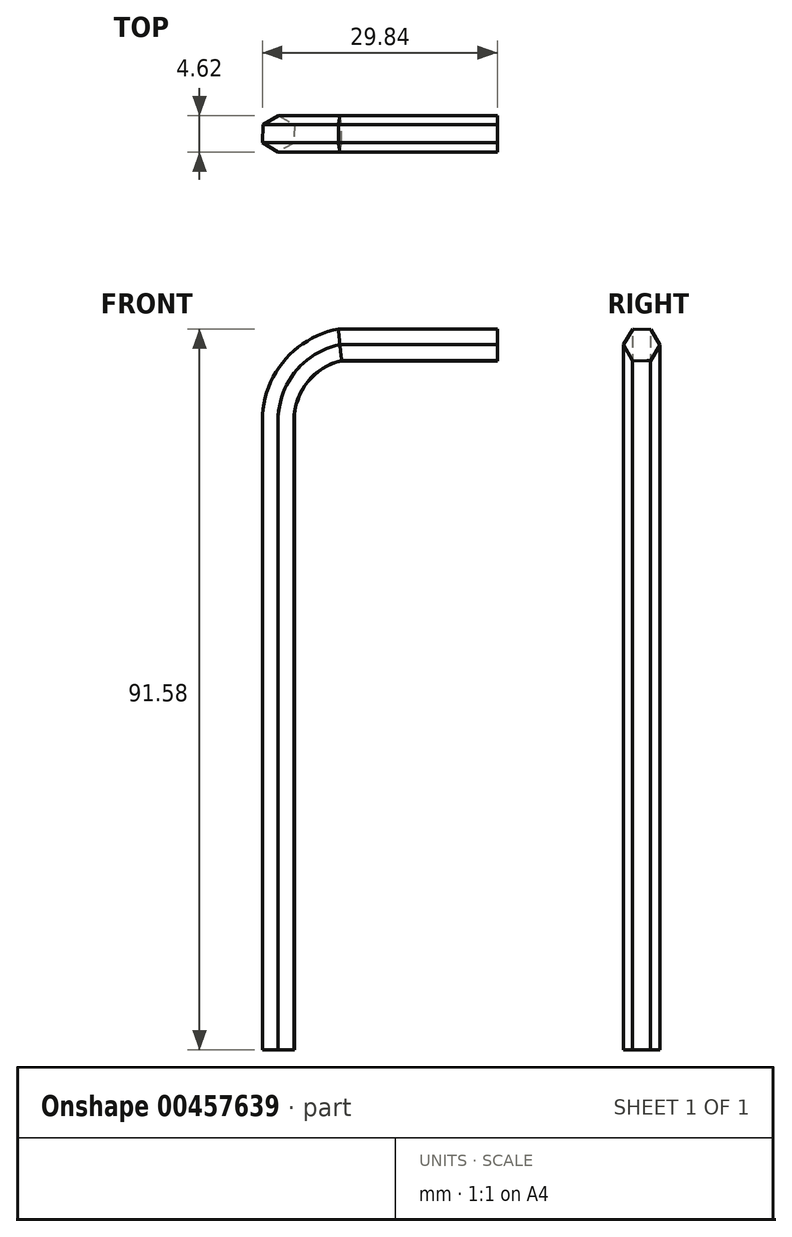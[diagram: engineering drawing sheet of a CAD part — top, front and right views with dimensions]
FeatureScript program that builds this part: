
annotation { "Feature Type Name" : "Feature", "Feature Type Description" : "" }
export const myFeature = defineFeature(function(context is Context, id is Id, definition is map)
    precondition{}
    {
        {
            var Q0;
            Q0=qCreatedBy(makeId("Top.planeOp"),FACE);
            var sketch = newSketch(context, id + "F0", { "sketchPlane" : qUnion([Q0])});
            skCircle(sketch, "E0.cCircle", {"center": v(0, 0) * mm, "radius": 2 * mm, "construction": true});
            skLineSegment(sketch, "E0.0", {"start": v(-1.98, 1.19) * mm, "end": v(0.04, 2.3) * mm});
            skLineSegment(sketch, "E0.1", {"start": v(0.04, 2.3) * mm, "end": v(2.02, 1.12) * mm});
            skLineSegment(sketch, "E0.2", {"start": v(2.02, 1.12) * mm, "end": v(1.98, -1.19) * mm});
            skLineSegment(sketch, "E0.3", {"start": v(1.98, -1.19) * mm, "end": v(-0.04, -2.3) * mm});
            skLineSegment(sketch, "E0.4", {"start": v(-0.04, -2.3) * mm, "end": v(-2.02, -1.12) * mm});
            skLineSegment(sketch, "E0.5", {"start": v(-2.02, -1.12) * mm, "end": v(-1.98, 1.19) * mm});
            skPoint(sketch, "E0.0.midPoint", {"position": v(-0.97, 1.75) * mm});
            skSolve(sketch);
        }
        {
            var Q0;
            Q0=qCreatedBy(makeId("Front.planeOp"),FACE);
            var sketch = newSketch(context, id + "F1", { "sketchPlane" : qUnion([Q0])});
            skLineSegment(sketch, "E1", {"start": v(0, 0) * mm, "end": v(0, 80) * mm});
            skArc(sketch, "E2", {"start": v(7.82, 89.56) * mm, "mid": v(2.2, 86.18) * mm, "end": v(0, 80) * mm});
            skLineSegment(sketch, "E3", {"start": v(7.82, 89.56) * mm, "end": v(27.82, 89.56) * mm});
            skSolve(sketch);
        }
        {
            var Q0;
            Q0=makeQuery(id+"F0.imprint","IMPRINT",FACE,{"disambiguationData":[TD([[makeQuery(id+"F0.imprint","IMPRINT",EDGE,{"derivedFrom":sQuery(id+"F0.wireOp",EDGE,"E0.0")}),-1.0]])]});
            var Q1;
            Q1=sQuery(id+"F1.wireOp",EDGE,"E1");
            var Q2;
            Q2=sQuery(id+"F1.wireOp",EDGE,"E2");
            var Q3;
            Q3=sQuery(id+"F1.wireOp",EDGE,"E3");
            sweep(context, id + "F2", {"profiles" : qUnion([Q0]), "path" : qUnion([Q1, Q2, Q3])});
        }
    });
